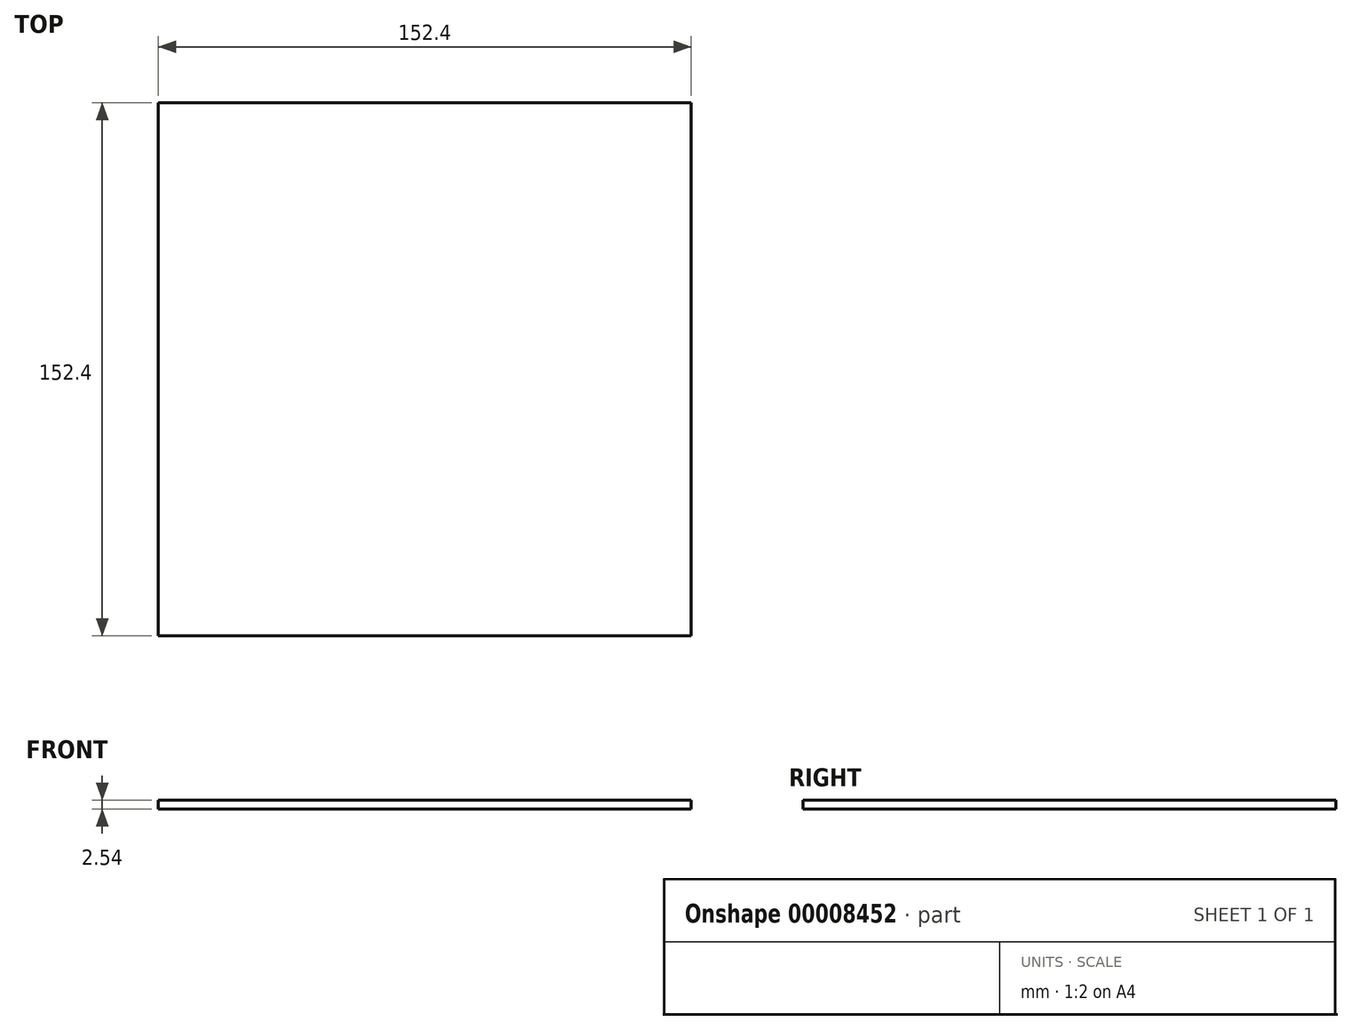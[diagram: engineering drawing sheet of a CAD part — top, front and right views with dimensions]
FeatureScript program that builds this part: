
annotation { "Feature Type Name" : "Feature", "Feature Type Description" : "" }
export const myFeature = defineFeature(function(context is Context, id is Id, definition is map)
    precondition{}
    {
        {
            var Q0;
            Q0=qCreatedBy(makeId("Top.planeOp"),FACE);
            var sketch = newSketch(context, id + "F0", { "sketchPlane" : qUnion([Q0])});
            skLineSegment(sketch, "E0.bottom", {"start": v(0, 0) * mm, "end": v(152.4, 0) * mm});
            skLineSegment(sketch, "E0.top", {"start": v(0, 152.4) * mm, "end": v(152.4, 152.4) * mm});
            skLineSegment(sketch, "E0.left", {"start": v(0, 0) * mm, "end": v(0, 152.4) * mm});
            skLineSegment(sketch, "E0.right", {"start": v(152.4, 0) * mm, "end": v(152.4, 152.4) * mm});
            skSolve(sketch);
        }
        {
            var Q0;
            Q0=makeQuery(id+"F0.imprint","IMPRINT",FACE,{"disambiguationData":[TD([[makeQuery(id+"F0.imprint","IMPRINT",EDGE,{"derivedFrom":sQuery(id+"F0.wireOp",EDGE,"E0.bottom")}),1.0]])]});
            extrude(context, id + "F1", {"entities" : qUnion([Q0]), "depth" : 2.54 * mm});
        }
    });
